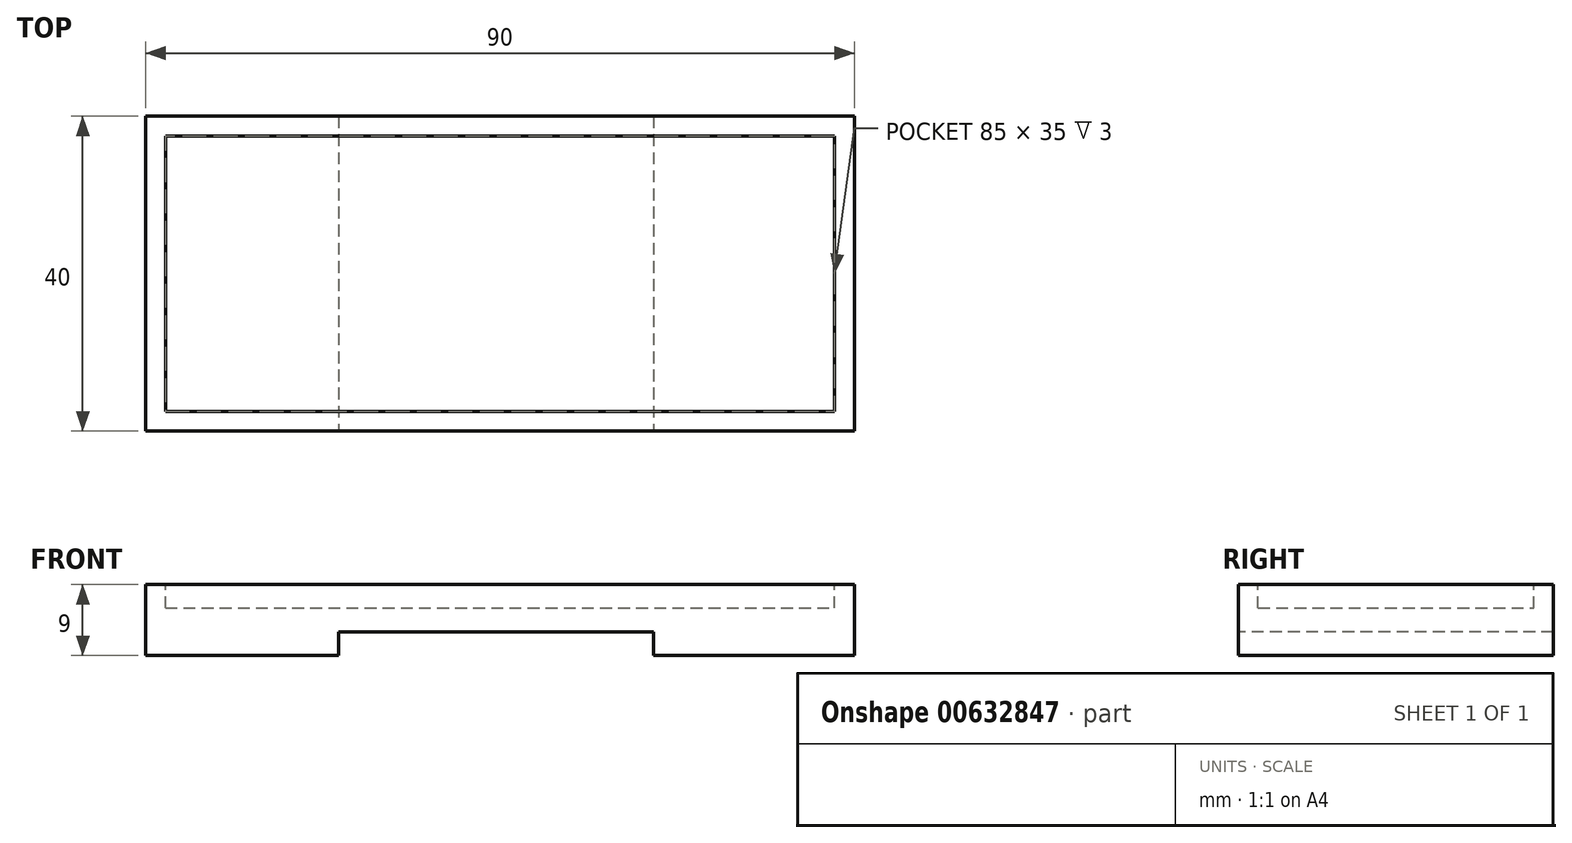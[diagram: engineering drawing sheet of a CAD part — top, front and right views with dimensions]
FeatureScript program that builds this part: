
annotation { "Feature Type Name" : "Feature", "Feature Type Description" : "" }
export const myFeature = defineFeature(function(context is Context, id is Id, definition is map)
    precondition{}
    {
        {
            var Q0;
            Q0=qCreatedBy(makeId("Front.planeOp"),FACE);
            var sketch = newSketch(context, id + "F0", { "sketchPlane" : qUnion([Q0])});
            skLineSegment(sketch, "E0.top", {"start": v(45, 3) * mm, "end": v(-45, 3) * mm});
            skLineSegment(sketch, "E0.left", {"start": v(45, -3) * mm, "end": v(45, 3) * mm});
            skLineSegment(sketch, "E0.right", {"start": v(-45, -3) * mm, "end": v(-45, 3) * mm});
            skPoint(sketch, "E0.middle", {"position": v(0, 0) * mm});
            skLineSegment(sketch, "E1", {"start": v(-20.51, -3) * mm, "end": v(-20.51, 0) * mm});
            skLineSegment(sketch, "E2", {"start": v(19.49, 0) * mm, "end": v(19.49, -3) * mm});
            skLineSegment(sketch, "E3", {"start": v(-20.51, 0) * mm, "end": v(19.49, 0) * mm});
            skLineSegment(sketch, "E4.trimOffspring", {"start": v(-20.51, -3) * mm, "end": v(-45, -3) * mm});
            skLineSegment(sketch, "E5", {"start": v(19.49, -3) * mm, "end": v(45, -3) * mm});
            skSolve(sketch);
        }
        {
            var Q0;
            Q0 = qSketchRegion(id + "F0", true);
            extrude(context, id + "F1", {"entities" : qUnion([Q0]), "depth" : 40 * mm, "offsetDistance" : 25 * mm});
        }
        {
            var Q0;
            Q0=makeQuery(id+"F1.opExtrude","SWEPT_FACE",FACE,{"disambiguationData":[OSD([sQuery(id+"F0.wireOp",EDGE,"E0.top")])]});
            var sketch = newSketch(context, id + "F2", { "sketchPlane" : qUnion([Q0])});
            skLineSegment(sketch, "E6.bottom", {"start": v(-41.93, -2) * mm, "end": v(42.07, -2) * mm});
            skLineSegment(sketch, "E6.top", {"start": v(-41.93, -38) * mm, "end": v(42.07, -38) * mm});
            skLineSegment(sketch, "E6.left", {"start": v(-41.93, -2) * mm, "end": v(-41.93, -38) * mm});
            skLineSegment(sketch, "E6.right", {"start": v(42.07, -2) * mm, "end": v(42.07, -38) * mm});
            skSolve(sketch);
        }
        {
            var Q0;
            Q0 = qSketchRegion(id + "F2", true);
            extrude(context, id + "F3", {"entities" : qUnion([Q0]), "operationType" : NewBodyOperationType.ADD, "depth" : -3 * mm, "offsetDistance" : 25 * mm});
        }
        {
            var Q0;
            Q0=makeQuery(id+"F1.opExtrude","SWEPT_FACE",FACE,{"disambiguationData":[OSD([sQuery(id+"F0.wireOp",EDGE,"E0.top")])]});
            shell(context, id + "F4", {"entities" : qUnion([Q0]), "thickness" : 2.5 * mm});
        }
        {
            var Q0;
            Q0=makeQuery(id+"F4.opShell","OFFSET_FACE",FACE,{"disambiguationData":[OSD([sQuery(id+"F0.wireOp",EDGE,"E3")])]});
            extrude(context, id + "F5", {"entities" : qUnion([Q0]), "operationType" : NewBodyOperationType.REMOVE, "oppositeDirection" : true, "depth" : 3 * mm, "offsetDistance" : 25 * mm});
        }
        {
            var Q0;
            Q0=qCreatedBy(makeId("Top.planeOp"),FACE);
            var sketch = newSketch(context, id + "F6", { "sketchPlane" : qUnion([Q0])});
            skLineSegment(sketch, "E7.bottom", {"start": v(-20.33, -40) * mm, "end": v(19.67, -40) * mm});
            skLineSegment(sketch, "E7.top", {"start": v(-20.33, 0) * mm, "end": v(19.67, 0) * mm});
            skLineSegment(sketch, "E7.left", {"start": v(-20.33, -40) * mm, "end": v(-20.33, 0) * mm});
            skLineSegment(sketch, "E7.right", {"start": v(19.67, -40) * mm, "end": v(19.67, 0) * mm});
            skSolve(sketch);
        }
        {
            var Q0;
            Q0=makeQuery(id+"F1.opExtrude","SWEPT_FACE",FACE,{"disambiguationData":[OSD([sQuery(id+"F0.wireOp",EDGE,"E4.trimOffspring")])]});
            var Q1;
            Q1=makeQuery(id+"F1.opExtrude","SWEPT_FACE",FACE,{"disambiguationData":[OSD([sQuery(id+"F0.wireOp",EDGE,"E5")])]});
            extrude(context, id + "F7", {"entities" : qUnion([Q0, Q1]), "operationType" : NewBodyOperationType.ADD, "depth" : 3 * mm, "offsetDistance" : 25 * mm});
        }
        {
            var Q0;
            Q0=makeQuery(id+"F6.imprint","IMPRINT",FACE,{"disambiguationData":[TD([[makeQuery(id+"F6.imprint","IMPRINT",EDGE,{"derivedFrom":sQuery(id+"F6.wireOp",EDGE,"E7.bottom")}),1.0]])]});
            extrude(context, id + "F8", {"entities" : qUnion([Q0]), "operationType" : NewBodyOperationType.ADD, "oppositeDirection" : true, "depth" : 3 * mm, "offsetDistance" : 25 * mm});
        }
        {
            var Q0;
            Q0=makeQuery(id+"F8.opExtrude","SWEPT_FACE",FACE,{"disambiguationData":[OSD([sQuery(id+"F6.wireOp",EDGE,"E7.left")])]});
            extrude(context, id + "F9", {"entities" : qUnion([Q0]), "operationType" : NewBodyOperationType.ADD, "depth" : .2 * mm, "offsetDistance" : 25 * mm});
        }
        {
            var Q0;
            Q0=makeQuery(id+"F5.boolean.opBoolean","MERGE",FACE,{"derivedFrom":[makeQuery(id+"F4.opShell","OFFSET_FACE",FACE,{"disambiguationData":[OSD([sQuery(id+"F0.wireOp",EDGE,"E4.trimOffspring")])]}),makeQuery(id+"F5.opExtrude","CAP_FACE",FACE,{"disambiguationData":[OSD([sQuery(id+"F0.wireOp",EDGE,"E3")])],"isStart":false})]});
            var Q1;
            Q1=makeQuery(id+"F5.boolean.opBoolean","MERGE",FACE,{"derivedFrom":[makeQuery(id+"F4.opShell","OFFSET_FACE",FACE,{"disambiguationData":[OSD([sQuery(id+"F0.wireOp",EDGE,"E5")])]}),makeQuery(id+"F5.opExtrude","CAP_FACE",FACE,{"disambiguationData":[OSD([sQuery(id+"F0.wireOp",EDGE,"E3")])],"isStart":false})]});
            extrude(context, id + "F10", {"entities" : qUnion([Q0, Q1]), "operationType" : NewBodyOperationType.ADD, "depth" : .5 * mm, "offsetDistance" : 25 * mm});
        }
    });
